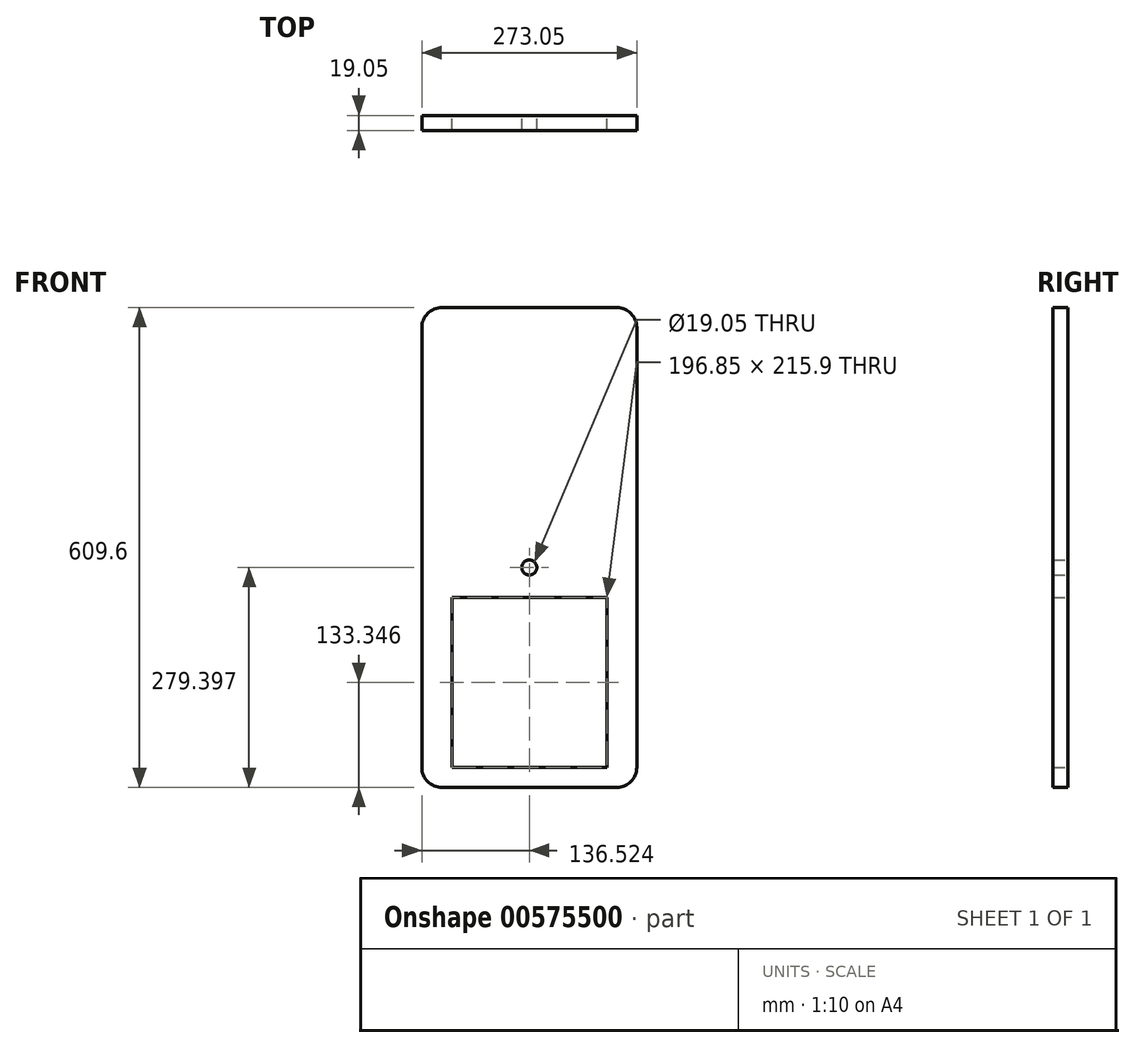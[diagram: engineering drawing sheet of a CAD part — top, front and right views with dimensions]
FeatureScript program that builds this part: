
annotation { "Feature Type Name" : "Feature", "Feature Type Description" : "" }
export const myFeature = defineFeature(function(context is Context, id is Id, definition is map)
    precondition{}
    {
        {
            var Q0;
            Q0=qCreatedBy(makeId("Front.planeOp"),FACE);
            var sketch = newSketch(context, id + "F0", { "sketchPlane" : qUnion([Q0])});
            skLineSegment(sketch, "E0.bottom", {"start": v(-92.1, 171.95) * mm, "end": v(-66.7, 171.95) * mm});
            skLineSegment(sketch, "E0.top", {"start": v(-66.7, -132.85) * mm, "end": v(-66.7, -132.85) * mm});
            skLineSegment(sketch, "E0.left", {"start": v(-92.1, 171.95) * mm, "end": v(-92.1, -107.45) * mm});
            skLineSegment(sketch, "E1.bottom", {"start": v(-66.7, -132.85) * mm, "end": v(104.75, -132.85) * mm});
            skLineSegment(sketch, "E1.left", {"start": v(-66.7, -132.85) * mm, "end": v(-66.7, -107.45) * mm});
            skLineSegment(sketch, "E1.right", {"start": v(104.75, -132.85) * mm, "end": v(104.75, -107.45) * mm});
            skLineSegment(sketch, "E2.bottom", {"start": v(104.75, -132.85) * mm, "end": v(155.55, -132.85) * mm});
            skLineSegment(sketch, "E2.top", {"start": v(155.55, 171.95) * mm, "end": v(180.95, 171.95) * mm});
            skLineSegment(sketch, "E2.right", {"start": v(180.95, -107.45) * mm, "end": v(180.95, 171.95) * mm});
            skLineSegment(sketch, "E3", {"start": v(-79.4, -132.85) * mm, "end": v(-79.4, 146.55) * mm});
            skLineSegment(sketch, "E4", {"start": v(95.22, -107.45) * mm, "end": v(95.22, -122.41) * mm});
            skLineSegment(sketch, "E5", {"start": v(-92.1, 171.95) * mm, "end": v(-92.1, 121.15) * mm});
            skLineSegment(sketch, "E6.bottom", {"start": v(-92.1, 171.95) * mm, "end": v(-15.9, 171.95) * mm});
            skLineSegment(sketch, "E6.top", {"start": v(-66.7, 476.75) * mm, "end": v(155.55, 476.75) * mm});
            skLineSegment(sketch, "E6.left", {"start": v(-92.1, 171.95) * mm, "end": v(-92.1, 451.35) * mm});
            skLineSegment(sketch, "E6.right", {"start": v(180.95, 171.95) * mm, "end": v(180.95, 451.35) * mm});
            skLineSegment(sketch, "E7.trimOffspring", {"start": v(104.75, 171.95) * mm, "end": v(180.95, 171.95) * mm});
            skPoint(sketch, "E8.visualSharp", {"position": v(-92.1, 476.75) * mm});
            skArc(sketch, "E8.filletArc", {"start": v(-66.7, 476.75) * mm, "mid": v(-84.66, 469.3) * mm, "end": v(-92.1, 451.35) * mm});
            skPoint(sketch, "E9.visualSharp", {"position": v(180.95, 476.75) * mm});
            skArc(sketch, "E9.filletArc", {"start": v(180.95, 451.35) * mm, "mid": v(173.5, 469.3) * mm, "end": v(155.55, 476.75) * mm});
            skPoint(sketch, "E10.visualSharp", {"position": v(180.95, -132.85) * mm});
            skArc(sketch, "E10.filletArc", {"start": v(155.55, -132.85) * mm, "mid": v(173.5, -125.41) * mm, "end": v(180.95, -107.45) * mm});
            skPoint(sketch, "E11.visualSharp", {"position": v(-92.1, -132.85) * mm});
            skArc(sketch, "E11.filletArc", {"start": v(-92.1, -107.45) * mm, "mid": v(-84.66, -125.41) * mm, "end": v(-66.7, -132.85) * mm});
            skLineSegment(sketch, "E12.filletArc", {"start": v(219.05, 95.75) * mm, "end": v(219.05, 95.75) * mm});
            skLineSegment(sketch, "E13.filletArc", {"start": v(-3.2, 95.75) * mm, "end": v(-3.2, 95.75) * mm});
            skPoint(sketch, "E14.newPointB", {"position": v(-15.9, -107.45) * mm});
            skLineSegment(sketch, "E14.filletArc", {"start": v(-3.2, -107.45) * mm, "end": v(-3.2, -107.45) * mm});
            skPoint(sketch, "E15.newPointB", {"position": v(206.35, -107.45) * mm});
            skLineSegment(sketch, "E15.filletArc", {"start": v(219.05, -107.45) * mm, "end": v(219.05, -107.45) * mm});
            skLineSegment(sketch, "E16", {"start": v(-92.1, 335.6) * mm, "end": v(180.95, 335.6) * mm});
            skLineSegment(sketch, "E17", {"start": v(180.95, 335.6) * mm, "end": v(44.42, 335.6) * mm});
            skLineSegment(sketch, "E18", {"start": v(44.42, 335.6) * mm, "end": v(44.42, 288.84) * mm});
            skLineSegment(sketch, "E19", {"start": v(180.95, 288.84) * mm, "end": v(44.42, 288.84) * mm});
            skLineSegment(sketch, "E20", {"start": v(-66.7, 171.95) * mm, "end": v(-66.7, 335.6) * mm});
            skLineSegment(sketch, "E21", {"start": v(-92.1, 146.55) * mm, "end": v(53.95, 146.55) * mm});
            skCircle(sketch, "E22", {"center": v(44.42, 146.55) * mm, "radius": 9.53 * mm});
            skPoint(sketch, "E23.orphan", {"position": v(180.95, 146.55) * mm});
            skLineSegment(sketch, "E24", {"start": v(-92.1, -12.62) * mm, "end": v(-54, -12.62) * mm});
            skLineSegment(sketch, "E25", {"start": v(39.5, -132.85) * mm, "end": v(39.5, -107.45) * mm});
            skLineSegment(sketch, "E26", {"start": v(39.5, -107.45) * mm, "end": v(180.95, -107.45) * mm});
            skLineSegment(sketch, "E27", {"start": v(180.95, -107.45) * mm, "end": v(142.85, -107.45) * mm});
            skLineSegment(sketch, "E28.bottom", {"start": v(142.85, -107.45) * mm, "end": v(-54, -107.45) * mm});
            skLineSegment(sketch, "E28.top", {"start": v(142.85, 108.45) * mm, "end": v(-54, 108.45) * mm});
            skLineSegment(sketch, "E28.left", {"start": v(142.85, -107.45) * mm, "end": v(142.85, 108.45) * mm});
            skLineSegment(sketch, "E28.right", {"start": v(-54, -107.45) * mm, "end": v(-54, 108.45) * mm});
            skSolve(sketch);
        }
        {
            var Q0;
            Q0 = qSketchRegion(id + "F0", true);
            extrude(context, id + "F1", {"entities" : qUnion([Q0]), "depth" : 19.05 * mm, "offsetDistance" : 25.4 * mm});
        }
    });
